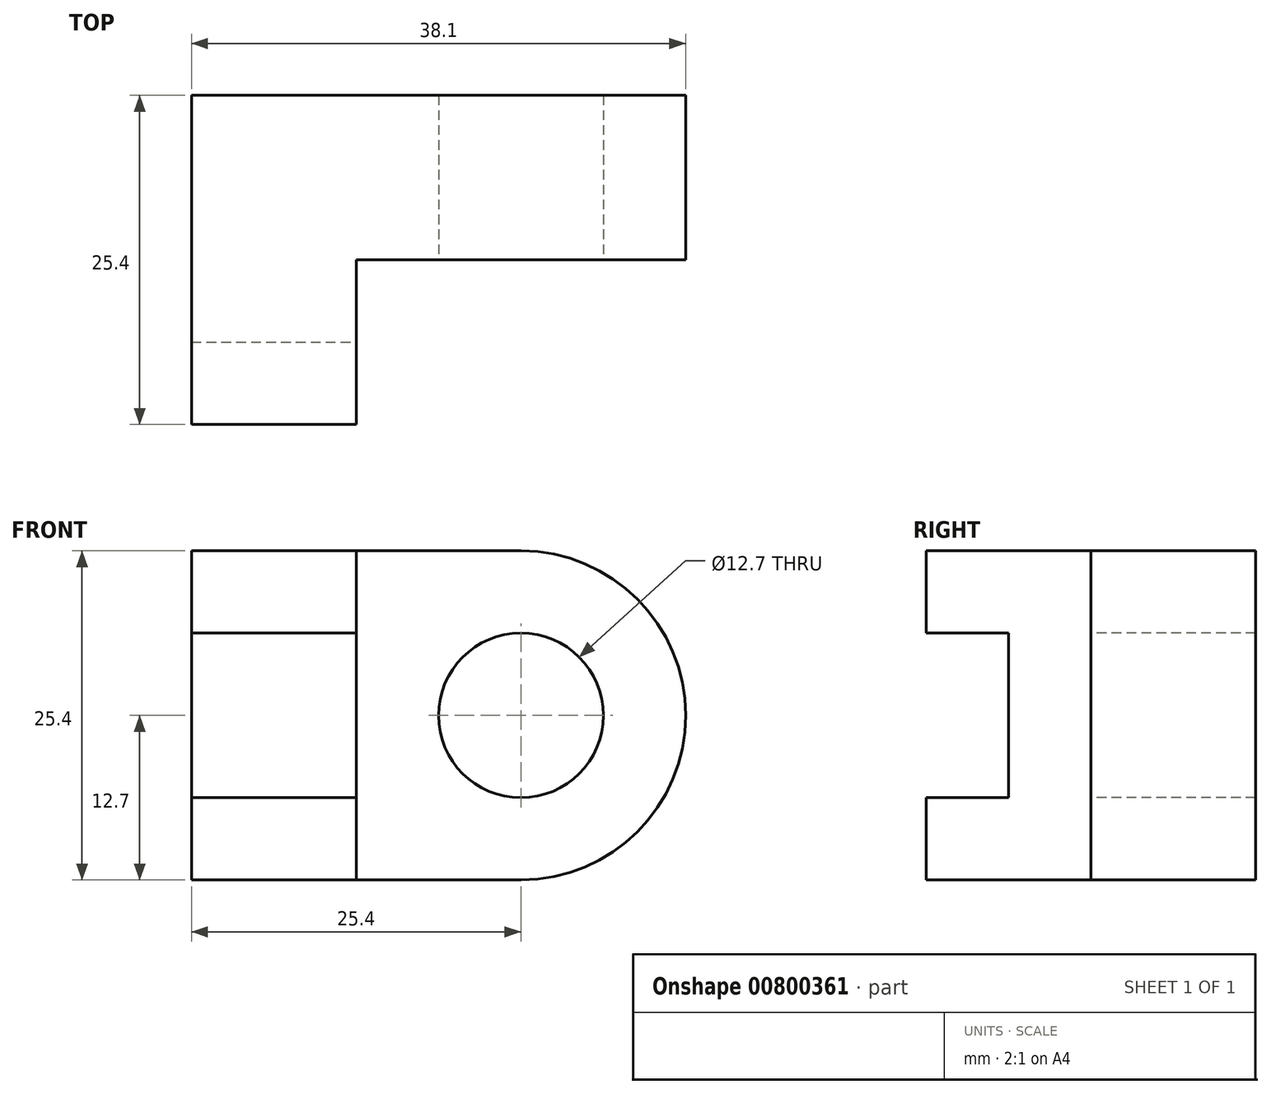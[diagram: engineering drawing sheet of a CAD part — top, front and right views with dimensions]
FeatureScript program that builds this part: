
annotation { "Feature Type Name" : "Feature", "Feature Type Description" : "" }
export const myFeature = defineFeature(function(context is Context, id is Id, definition is map)
    precondition{}
    {
        {
            var Q0;
            Q0=qCreatedBy(makeId("Front.planeOp"),FACE);
            var sketch = newSketch(context, id + "F0", { "sketchPlane" : qUnion([Q0])});
            skLineSegment(sketch, "E0", {"start": v(0, 0) * mm, "end": v(25.4, 0) * mm});
            skLineSegment(sketch, "E1", {"start": v(25.4, 0) * mm, "end": v(25.4, 25.4) * mm, "construction": true});
            skLineSegment(sketch, "E2", {"start": v(25.4, 25.4) * mm, "end": v(0, 25.4) * mm});
            skLineSegment(sketch, "E3", {"start": v(0, 25.4) * mm, "end": v(0, 0) * mm});
            skArc(sketch, "E4", {"start": v(25.4, 0) * mm, "mid": v(38.1, 12.7) * mm, "end": v(25.4, 25.4) * mm});
            skSolve(sketch);
        }
        {
            var Q0;
            Q0 = qSketchRegion(id + "F0", true);
            extrude(context, id + "F1", {"entities" : qUnion([Q0]), "depth" : 12.7 * mm, "offsetDistance" : 25.4 * mm});
        }
        {
            var Q0;
            Q0=makeQuery(id+"F1.opExtrude","CAP_FACE",FACE,{"disambiguationData":[OSD([sQuery(id+"F0.wireOp",EDGE,"E0"),sQuery(id+"F0.wireOp",EDGE,"E2"),sQuery(id+"F0.wireOp",EDGE,"E3"),sQuery(id+"F0.wireOp",EDGE,"E4")])],"isStart":false});
            var sketch = newSketch(context, id + "F2", { "sketchPlane" : qUnion([Q0])});
            skLineSegment(sketch, "E5", {"start": v(0, 25.4) * mm, "end": v(0, 19.05) * mm});
            skLineSegment(sketch, "E6", {"start": v(0, 19.05) * mm, "end": v(12.7, 19.05) * mm});
            skLineSegment(sketch, "E7", {"start": v(12.7, 19.05) * mm, "end": v(12.7, 25.4) * mm});
            skLineSegment(sketch, "E8", {"start": v(0, 0) * mm, "end": v(0, 6.35) * mm});
            skLineSegment(sketch, "E9", {"start": v(0, 6.35) * mm, "end": v(12.7, 6.35) * mm});
            skLineSegment(sketch, "E10", {"start": v(12.7, 6.35) * mm, "end": v(12.7, 0) * mm});
            skSolve(sketch);
        }
        {
            var Q0;
            {var subQ0=sQuery(id+"F2.wireOp",EDGE,"E5");Q0=makeQuery(id+"F2.imprint","IMPRINT",FACE,{"disambiguationData":[TD([[makeQuery(id+"F2.imprint","IMPRINT",EDGE,{"derivedFrom":subQ0}),1.0]])]});}
            var Q1;
            {var subQ0=sQuery(id+"F2.wireOp",EDGE,"E8");Q1=makeQuery(id+"F2.imprint","IMPRINT",FACE,{"disambiguationData":[TD([[makeQuery(id+"F2.imprint","IMPRINT",EDGE,{"derivedFrom":subQ0}),1.0]])]});}
            extrude(context, id + "F3", {"entities" : qUnion([Q0, Q1]), "operationType" : NewBodyOperationType.ADD, "depth" : 12.7 * mm, "offsetDistance" : 25.4 * mm});
        }
        {
            var Q0;
            Q0=makeQuery(id+"F1.opExtrude","CAP_FACE",FACE,{"disambiguationData":[OSD([sQuery(id+"F0.wireOp",EDGE,"E0"),sQuery(id+"F0.wireOp",EDGE,"E2"),sQuery(id+"F0.wireOp",EDGE,"E3"),sQuery(id+"F0.wireOp",EDGE,"E4")])],"isStart":false});
            var sketch = newSketch(context, id + "F4", { "sketchPlane" : qUnion([Q0])});
            skLineSegment(sketch, "E11", {"start": v(12.7, 19.05) * mm, "end": v(12.7, 6.35) * mm});
            skSolve(sketch);
        }
        {
            var Q0;
            Q0=makeQuery(id+"F4.imprint","IMPRINT",FACE,{"disambiguationData":[TD([[makeQuery(id+"F4.imprint","IMPRINT",EDGE,{"derivedFrom":sQuery(id+"F4.wireOp",EDGE,"E11")}),-1.0]])]});
            extrude(context, id + "F5", {"entities" : qUnion([Q0]), "operationType" : NewBodyOperationType.ADD, "depth" : 6.35 * mm, "offsetDistance" : 25.4 * mm});
        }
        {
            var Q0;
            Q0=makeQuery(id+"F1.opExtrude","CAP_FACE",FACE,{"disambiguationData":[OSD([sQuery(id+"F0.wireOp",EDGE,"E0"),sQuery(id+"F0.wireOp",EDGE,"E2"),sQuery(id+"F0.wireOp",EDGE,"E3"),sQuery(id+"F0.wireOp",EDGE,"E4")])],"isStart":false});
            var sketch = newSketch(context, id + "F6", { "sketchPlane" : qUnion([Q0])});
            skLineSegment(sketch, "E12", {"start": v(25.4, 25.4) * mm, "end": v(25.4, 12.7) * mm, "construction": true});
            skCircle(sketch, "E13", {"center": v(25.4, 12.7) * mm, "radius": 6.35 * mm});
            skSolve(sketch);
        }
        {
            var Q0;
            Q0=makeQuery(id+"F6.imprint","IMPRINT",FACE,{"disambiguationData":[TD([[makeQuery(id+"F6.imprint","IMPRINT",EDGE,{"derivedFrom":sQuery(id+"F6.wireOp",EDGE,"E13")}),1.0]])]});
            extrude(context, id + "F7", {"entities" : qUnion([Q0]), "operationType" : NewBodyOperationType.REMOVE, "endBound" : BoundingType.THROUGH_ALL, "oppositeDirection" : true, "depth" : 25.4 * mm, "offsetDistance" : 25.4 * mm});
        }
    });
